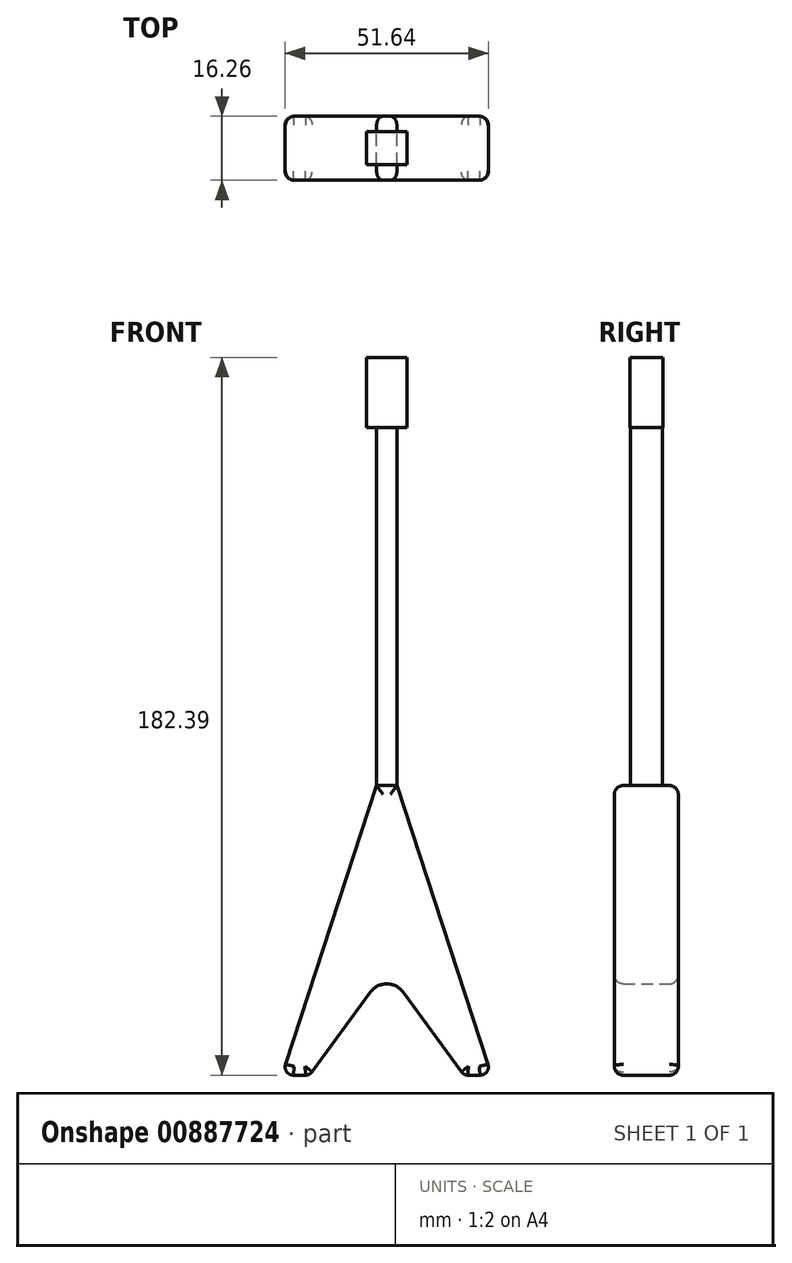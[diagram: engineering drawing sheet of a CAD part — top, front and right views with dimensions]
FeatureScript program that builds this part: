
annotation { "Feature Type Name" : "Feature", "Feature Type Description" : "" }
export const myFeature = defineFeature(function(context is Context, id is Id, definition is map)
    precondition{}
    {
        {
            var Q0;
            Q0=qCreatedBy(makeId("Front.planeOp"),FACE);
            var sketch = newSketch(context, id + "F0", { "sketchPlane" : qUnion([Q0])});
            skLineSegment(sketch, "E0.bottom", {"start": v(0, 134.92) * mm, "end": v(-5.14, 134.92) * mm});
            skLineSegment(sketch, "E0.top", {"start": v(0, 117.05) * mm, "end": v(-5.14, 117.05) * mm});
            skLineSegment(sketch, "E0.left", {"start": v(0, 134.92) * mm, "end": v(0, 117.05) * mm});
            skLineSegment(sketch, "E0.right", {"start": v(-5.14, 134.92) * mm, "end": v(-5.14, 117.05) * mm});
            skLineSegment(sketch, "E1", {"start": v(-2.57, 117.05) * mm, "end": v(-2.57, 26.12) * mm});
            skPoint(sketch, "E1.endSnap0", {"position": v(-2.57, 117.05) * mm});
            skLineSegment(sketch, "E2", {"start": v(-2.57, 26.12) * mm, "end": v(-26.62, -47.47) * mm});
            skLineSegment(sketch, "E3", {"start": v(-26.62, -47.47) * mm, "end": v(-19.58, -47.47) * mm});
            skLineSegment(sketch, "E4", {"start": v(-19.58, -47.47) * mm, "end": v(0, -20.75) * mm});
            skLineSegment(sketch, "E5", {"start": v(0, 117.05) * mm, "end": v(0, -20.75) * mm});
            skLineSegment(sketch, "E6.MirrorCS", {"start": v(2.57, 117.05) * mm, "end": v(2.57, 26.12) * mm});
            skLineSegment(sketch, "E7.MirrorCS", {"start": v(2.57, 26.12) * mm, "end": v(26.62, -47.47) * mm});
            skLineSegment(sketch, "E8.MirrorCS", {"start": v(26.62, -47.47) * mm, "end": v(19.58, -47.47) * mm});
            skLineSegment(sketch, "E9.MirrorCS", {"start": v(19.58, -47.47) * mm, "end": v(0, -20.75) * mm});
            skLineSegment(sketch, "E10.MirrorCS", {"start": v(5.14, 134.92) * mm, "end": v(5.14, 117.05) * mm});
            skLineSegment(sketch, "E11.MirrorCS", {"start": v(0, 117.05) * mm, "end": v(5.14, 117.05) * mm});
            skLineSegment(sketch, "E12.MirrorCS", {"start": v(0, 134.92) * mm, "end": v(5.14, 134.92) * mm});
            skLineSegment(sketch, "E13", {"start": v(-2.57, 26.12) * mm, "end": v(2.57, 26.12) * mm});
            skSolve(sketch);
        }
        {
            var Q0;
            {var subQ4=sQuery(id+"F0.wireOp",EDGE,"E2");Q0=makeQuery(id+"F0.imprint","IMPRINT",FACE,{"disambiguationData":[TD([[makeQuery(id+"F0.imprint","IMPRINT",EDGE,{"derivedFrom":subQ4}),1.0]])]});}
            var Q1;
            {var subQ1=sQuery(id+"F0.wireOp",EDGE,"E7.MirrorCS");Q1=makeQuery(id+"F0.imprint","IMPRINT",FACE,{"disambiguationData":[TD([[makeQuery(id+"F0.imprint","IMPRINT",EDGE,{"derivedFrom":subQ1}),-1.0]])]});}
            extrude(context, id + "F1", {"entities" : qUnion([Q0, Q1]), "endBound" : BoundingType.SYMMETRIC, "depth" : 16.26 * mm, "offsetDistance" : 25.4 * mm});
        }
        {
            var Q0;
            {var subQ3=sQuery(id+"F0.wireOp",EDGE,"E1");Q0=makeQuery(id+"F0.imprint","IMPRINT",FACE,{"disambiguationData":[TD([[makeQuery(id+"F0.imprint","IMPRINT",EDGE,{"derivedFrom":subQ3}),1.0]])]});}
            var Q1;
            {var subQ5=sQuery(id+"F0.wireOp",EDGE,"E6.MirrorCS");Q1=makeQuery(id+"F0.imprint","IMPRINT",FACE,{"disambiguationData":[TD([[makeQuery(id+"F0.imprint","IMPRINT",EDGE,{"derivedFrom":subQ5}),-1.0]])]});}
            extrude(context, id + "F2", {"entities" : qUnion([Q0, Q1]), "operationType" : NewBodyOperationType.ADD, "endBound" : BoundingType.SYMMETRIC, "depth" : 8.13 * mm, "offsetDistance" : 25.4 * mm});
        }
        {
            var Q0;
            Q0=makeQuery(id+"F0.imprint","IMPRINT",FACE,{"disambiguationData":[TD([[makeQuery(id+"F0.imprint","IMPRINT",EDGE,{"derivedFrom":sQuery(id+"F0.wireOp",EDGE,"E0.bottom")}),1.0]])]});
            var Q1;
            {var subQ3=sQuery(id+"F0.wireOp",EDGE,"E0.left");Q1=makeQuery(id+"F0.imprint","IMPRINT",FACE,{"disambiguationData":[TD([[makeQuery(id+"F0.imprint","IMPRINT",EDGE,{"derivedFrom":subQ3}),1.0]])]});}
            extrude(context, id + "F3", {"entities" : qUnion([Q0, Q1]), "operationType" : NewBodyOperationType.ADD, "endBound" : BoundingType.SYMMETRIC, "depth" : 8.38 * mm, "offsetDistance" : 25.4 * mm});
        }
        {
            var Q0;
            Q0=makeQuery(id+"F1.opExtrude","SWEPT_EDGE",EDGE,{"disambiguationData":[OSD([sQuery(id+"F0.wireOp",EDGE,"E2"),sQuery(id+"F0.wireOp",EDGE,"E3")])]});
            var Q1;
            Q1=makeQuery(id+"F1.opExtrude","SWEPT_EDGE",EDGE,{"disambiguationData":[OSD([sQuery(id+"F0.wireOp",EDGE,"E3"),sQuery(id+"F0.wireOp",EDGE,"E4")])]});
            var Q2;
            Q2=makeQuery(id+"F1.opExtrude","SWEPT_EDGE",EDGE,{"disambiguationData":[OSD([sQuery(id+"F0.wireOp",EDGE,"E8.MirrorCS"),sQuery(id+"F0.wireOp",EDGE,"E9.MirrorCS")])]});
            var Q3;
            Q3=makeQuery(id+"F1.opExtrude","SWEPT_EDGE",EDGE,{"disambiguationData":[OSD([sQuery(id+"F0.wireOp",EDGE,"E7.MirrorCS"),sQuery(id+"F0.wireOp",EDGE,"E8.MirrorCS")])]});
            fillet(context, id + "F4", {"entities" : qUnion([Q0, Q1, Q2, Q3]), "radius" : 2.1 * mm, "tangentPropagation" : true, "allowEdgeOverflow" : false});
        }
        {
            var Q0;
            Q0=makeQuery(id+"F1.opExtrude","SWEPT_EDGE",EDGE,{"disambiguationData":[OSD([sQuery(id+"F0.wireOp",EDGE,"E4"),sQuery(id+"F0.wireOp",EDGE,"E5"),sQuery(id+"F0.wireOp",EDGE,"E9.MirrorCS")])]});
            fillet(context, id + "F5", {"entities" : qUnion([Q0]), "radius" : 5.08 * mm, "tangentPropagation" : true, "allowEdgeOverflow" : false});
        }
        {
            var Q0;
            Q0=makeQuery(id+"F1.opExtrude","CAP_FACE",FACE,{"disambiguationData":[OSD([sQuery(id+"F0.wireOp",EDGE,"E2"),sQuery(id+"F0.wireOp",EDGE,"E3"),sQuery(id+"F0.wireOp",EDGE,"E4"),sQuery(id+"F0.wireOp",EDGE,"E7.MirrorCS"),sQuery(id+"F0.wireOp",EDGE,"E8.MirrorCS"),sQuery(id+"F0.wireOp",EDGE,"E9.MirrorCS"),sQuery(id+"F0.wireOp",EDGE,"E13")])],"isStart":false});
            var Q1;
            Q1=makeQuery(id+"F1.opExtrude","CAP_FACE",FACE,{"disambiguationData":[OSD([sQuery(id+"F0.wireOp",EDGE,"E2"),sQuery(id+"F0.wireOp",EDGE,"E3"),sQuery(id+"F0.wireOp",EDGE,"E4"),sQuery(id+"F0.wireOp",EDGE,"E7.MirrorCS"),sQuery(id+"F0.wireOp",EDGE,"E8.MirrorCS"),sQuery(id+"F0.wireOp",EDGE,"E9.MirrorCS"),sQuery(id+"F0.wireOp",EDGE,"E13")])],"isStart":true});
            fillet(context, id + "F6", {"entities" : qUnion([Q0, Q1]), "radius" : 2.27 * mm, "tangentPropagation" : true, "allowEdgeOverflow" : false});
        }
    });
